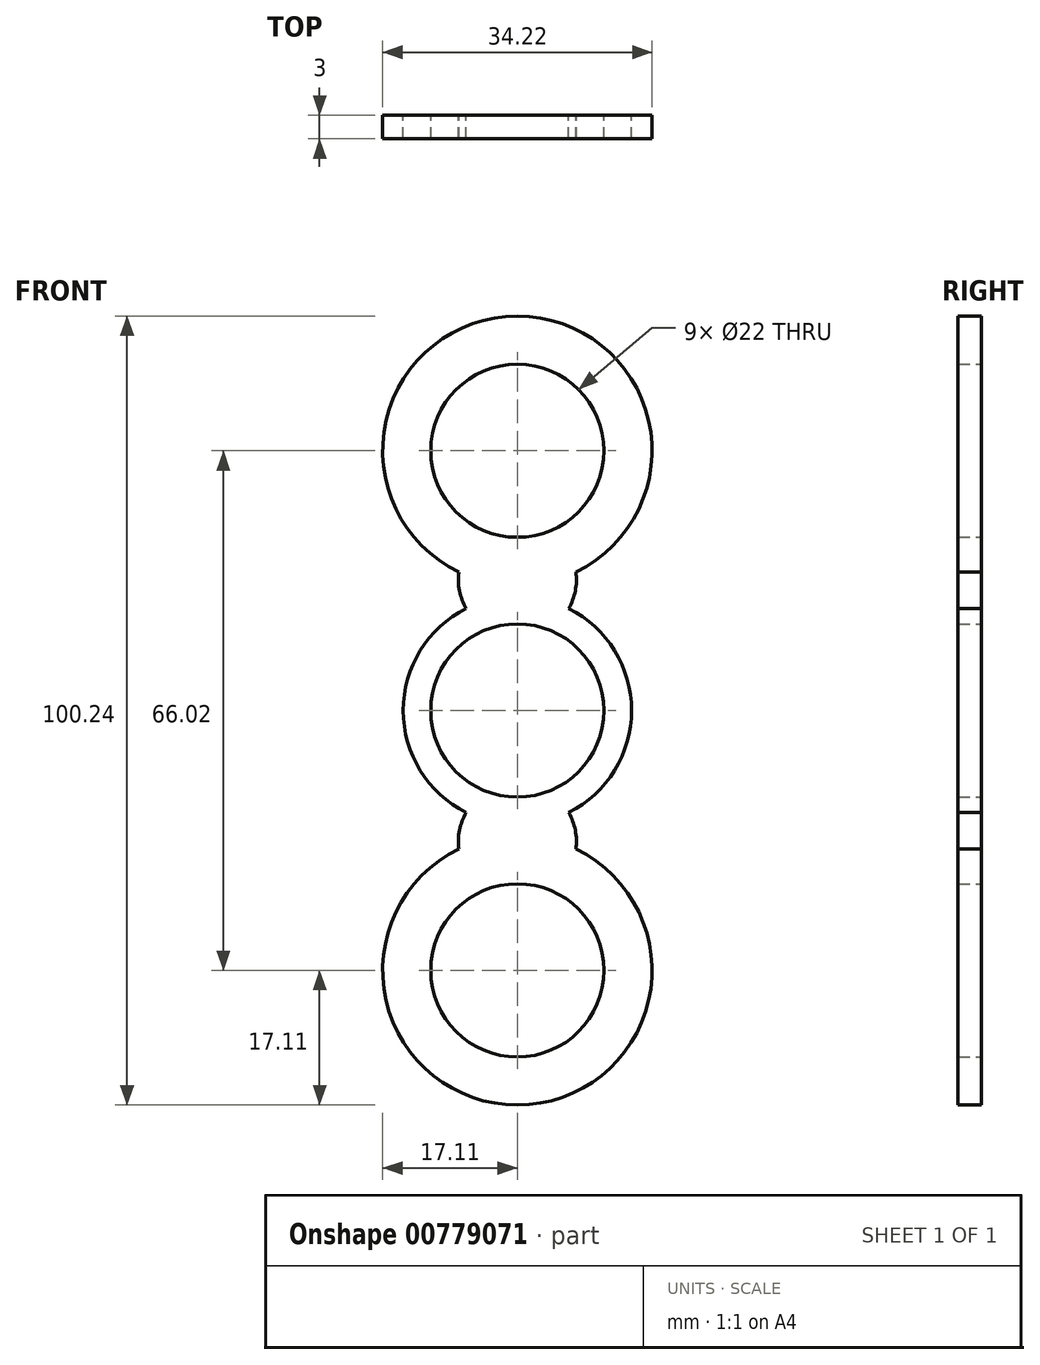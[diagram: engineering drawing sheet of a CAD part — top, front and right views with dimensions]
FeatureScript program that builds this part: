
annotation { "Feature Type Name" : "Feature", "Feature Type Description" : "" }
export const myFeature = defineFeature(function(context is Context, id is Id, definition is map)
    precondition{}
    {
        {
            var Q0;
            Q0=qCreatedBy(makeId("Front.planeOp"),FACE);
            var sketch = newSketch(context, id + "F0", { "sketchPlane" : qUnion([Q0])});
            skCircle(sketch, "E0", {"center": v(0, 0) * mm, "radius": 11 * mm});
            skArc(sketch, "E1", {"start": v(-7.44, 17.6) * mm, "mid": v(-7.36, 15.2) * mm, "end": v(-6.52, 12.95) * mm});
            skArc(sketch, "E2", {"start": v(7.44, 17.6) * mm, "mid": v(0, 50.12) * mm, "end": v(-7.44, 17.6) * mm});
            skCircle(sketch, "E3", {"center": v(0, 33.01) * mm, "radius": 11 * mm});
            skArc(sketch, "E4.trimOffspring", {"start": v(6.52, 12.95) * mm, "mid": v(7.36, 15.2) * mm, "end": v(7.44, 17.6) * mm});
            skArc(sketch, "E5.MirrorCS", {"start": v(-7.44, -17.6) * mm, "mid": v(-7.36, -15.2) * mm, "end": v(-6.52, -12.95) * mm});
            skArc(sketch, "E6.MirrorCS", {"start": v(6.52, -12.95) * mm, "mid": v(7.36, -15.2) * mm, "end": v(7.44, -17.6) * mm});
            skCircle(sketch, "E7.MirrorC", {"center": v(0, -33.01) * mm, "radius": 11 * mm});
            skArc(sketch, "E8.MirrorCS", {"start": v(7.44, -17.6) * mm, "mid": v(0, -50.12) * mm, "end": v(-7.44, -17.6) * mm});
            skArc(sketch, "E9", {"start": v(6.52, -12.95) * mm, "mid": v(14.5, 0) * mm, "end": v(6.52, 12.95) * mm});
            skPoint(sketch, "E10.orphan", {"position": v(-3.93, 10.27) * mm});
            skPoint(sketch, "E11.orphan", {"position": v(3.93, 10.27) * mm});
            skPoint(sketch, "E12.orphan", {"position": v(3.93, -10.27) * mm});
            skPoint(sketch, "E13.orphan", {"position": v(-3.93, -10.27) * mm});
            skArc(sketch, "E14.trimOffspring", {"start": v(-6.52, 12.95) * mm, "mid": v(-14.5, 0) * mm, "end": v(-6.52, -12.95) * mm});
            skSolve(sketch);
        }
        {
            var Q0;
            Q0=makeQuery(id+"F0.imprint","IMPRINT",FACE,{"disambiguationData":[TD([[makeQuery(id+"F0.imprint","IMPRINT",EDGE,{"derivedFrom":sQuery(id+"F0.wireOp",EDGE,"E1")}),1.0]])]});
            extrude(context, id + "F1", {"entities" : qUnion([Q0]), "depth" : 3 * mm, "offsetDistance" : 25 * mm});
        }
    });
